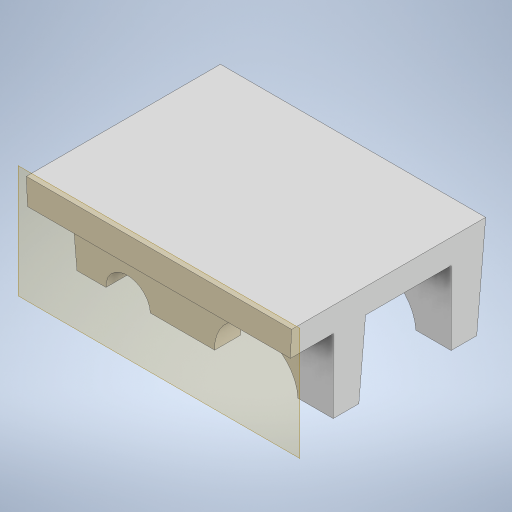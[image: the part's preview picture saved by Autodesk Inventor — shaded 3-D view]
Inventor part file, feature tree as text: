
AUTODESK INVENTOR PART (.ipt)
format: ipt  version: 2023 (Build 270158000, 158)  size: 285,696 bytes
history: native  units: in
note: dims shown in document units (in); Inventor stores cm internally (conversion verified against a paired STEP export)
features: extrude x3, sketch x2, plane x1, draft x1
ambient origin geometry x8: Origin, YZ Plane, XZ Plane, XY Plane, X Axis, Y Axis, Z Axis, Center Point
bodies: Solid1 (feature_tree)
feature tree (7):
  extrude  "Extrusion1"  Depth=5.0in
  extrude  "Extrusion2"  Depth=0.5in
  plane  "Work Plane1"
  sketch  "Sketch5"  dims[d3=7.4in d4=0.0in d15=1.4in d16=3.7in d17=6.0in d18=0.5in d20=2.528in d21=7.4in d22=0.0in d25=1.5in d26=0.866in d31=1.2546in d32=0.5669in d33=2.0in d34=1.5in d35=0.0172in d36=9.0in d37=0.0in d27=0.5in d28=0.0344in d29=0.0in d30=0.0in d38=0.5in d39=0.0344in]
  draft  "FaceDraft1"
  extrude  "Extrusion5"  Depth=0.5in
  sketch  "Sketch1"  dims[d0=5.0in d2=1.625in]
